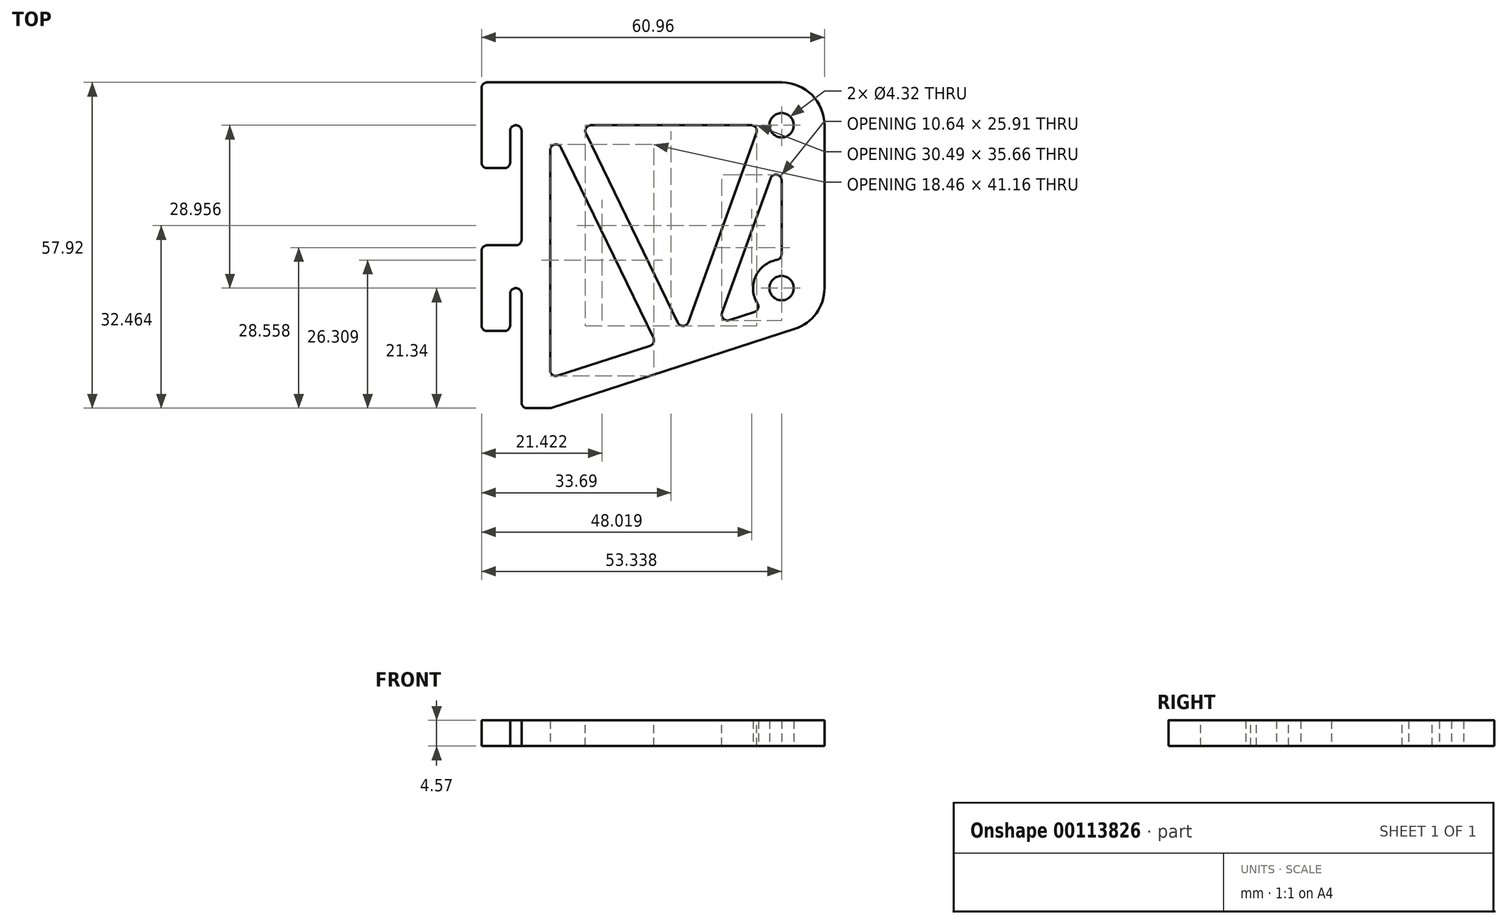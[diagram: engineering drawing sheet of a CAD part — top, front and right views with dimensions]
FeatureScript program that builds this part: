
annotation { "Feature Type Name" : "Feature", "Feature Type Description" : "" }
export const myFeature = defineFeature(function(context is Context, id is Id, definition is map)
    precondition{}
    {
        {
            var Q0;
            Q0=qCreatedBy(makeId("Top.planeOp"),FACE);
            var sketch = newSketch(context, id + "F0", { "sketchPlane" : qUnion([Q0])});
            skLineSegment(sketch, "E0", {"start": v(-7.11, 28.96) * mm, "end": v(-7.11, 13.72) * mm});
            skLineSegment(sketch, "E1", {"start": v(-7.11, 13.72) * mm, "end": v(-2.03, 13.72) * mm});
            skLineSegment(sketch, "E2", {"start": v(-2.03, 13.72) * mm, "end": v(-2.03, 21.34) * mm});
            skLineSegment(sketch, "E3", {"start": v(-2.03, 21.34) * mm, "end": v(0, 21.34) * mm});
            skLineSegment(sketch, "E4", {"start": v(0, 21.34) * mm, "end": v(0, 0) * mm});
            skLineSegment(sketch, "E5", {"start": v(0, 0) * mm, "end": v(-7.11, 0) * mm});
            skLineSegment(sketch, "E6", {"start": v(-7.11, 0) * mm, "end": v(-7.11, -15.24) * mm});
            skLineSegment(sketch, "E7", {"start": v(-7.11, -15.24) * mm, "end": v(-2.03, -15.24) * mm});
            skLineSegment(sketch, "E8", {"start": v(-2.03, -15.24) * mm, "end": v(-2.03, -7.62) * mm});
            skLineSegment(sketch, "E9", {"start": v(-2.03, -7.62) * mm, "end": v(0, -7.62) * mm});
            skLineSegment(sketch, "E10", {"start": v(0, -7.62) * mm, "end": v(0, -28.96) * mm});
            skPoint(sketch, "E11", {"position": v(0, 0) * mm});
            skPoint(sketch, "E12", {"position": v(-7.11, 21.34) * mm});
            skLineSegment(sketch, "E13", {"start": v(-7.11, 28.96) * mm, "end": v(46.23, 28.96) * mm});
            skLineSegment(sketch, "E14", {"start": v(0, -28.96) * mm, "end": v(5.08, -28.96) * mm});
            skLineSegment(sketch, "E15", {"start": v(5.08, -28.96) * mm, "end": v(48.58, -14.87) * mm});
            skCircle(sketch, "E16", {"center": v(46.23, 21.34) * mm, "radius": 2.16 * mm});
            skCircle(sketch, "E17", {"center": v(46.23, -7.62) * mm, "radius": 2.16 * mm});
            skLineSegment(sketch, "E18", {"start": v(46.23, 21.34) * mm, "end": v(46.23, 28.96) * mm, "construction": true});
            skLineSegment(sketch, "E19", {"start": v(46.23, 21.34) * mm, "end": v(53.85, 21.34) * mm, "construction": true});
            skArc(sketch, "E20", {"start": v(53.85, 21.34) * mm, "mid": v(51.62, 26.72) * mm, "end": v(46.23, 28.96) * mm});
            skLineSegment(sketch, "E21", {"start": v(53.85, 21.34) * mm, "end": v(53.85, -7.62) * mm});
            skLineSegment(sketch, "E22", {"start": v(53.85, -7.62) * mm, "end": v(46.23, -7.62) * mm, "construction": true});
            skLineSegment(sketch, "E23", {"start": v(48.58, -14.87) * mm, "end": v(46.23, -7.62) * mm, "construction": true});
            skArc(sketch, "E24", {"start": v(48.58, -14.87) * mm, "mid": v(52.4, -12.1) * mm, "end": v(53.85, -7.62) * mm});
            skLineSegment(sketch, "E25", {"start": v(5.08, 21.34) * mm, "end": v(5.08, -23.62) * mm});
            skPoint(sketch, "E25.startSnap0", {"position": v(-1.02, 21.34) * mm});
            skLineSegment(sketch, "E26", {"start": v(5.08, -23.62) * mm, "end": v(23.95, -17.5) * mm});
            skLineSegment(sketch, "E27", {"start": v(23.95, -17.5) * mm, "end": v(5.08, 21.34) * mm});
            skLineSegment(sketch, "E28", {"start": v(10.73, 21.34) * mm, "end": v(28.83, -15.92) * mm});
            skLineSegment(sketch, "E29", {"start": v(28.83, -15.92) * mm, "end": v(42.26, 21.34) * mm});
            skLineSegment(sketch, "E30", {"start": v(42.26, 21.34) * mm, "end": v(10.73, 21.34) * mm});
            skLineSegment(sketch, "E31", {"start": v(46.23, -2.54) * mm, "end": v(46.23, 17.37) * mm});
            skLineSegment(sketch, "E32", {"start": v(46.23, 17.37) * mm, "end": v(34.95, -13.94) * mm});
            skLineSegment(sketch, "E33", {"start": v(34.95, -13.94) * mm, "end": v(42.83, -11.4) * mm});
            skArc(sketch, "E34", {"start": v(46.23, -2.54) * mm, "mid": v(41.49, -5.8) * mm, "end": v(42.83, -11.4) * mm});
            skLineSegment(sketch, "E35", {"start": v(5.08, -23.62) * mm, "end": v(42.83, -11.4) * mm, "construction": true});
            skLineSegment(sketch, "E36", {"start": v(15.21, 0.49) * mm, "end": v(19.78, 2.7) * mm, "construction": true});
            skLineSegment(sketch, "E37", {"start": v(35.55, 2.7) * mm, "end": v(40.32, 0.98) * mm, "construction": true});
            skPoint(sketch, "E38", {"position": v(35.55, 2.7) * mm});
            skPoint(sketch, "E39", {"position": v(19.78, 2.7) * mm});
            skLineSegment(sketch, "E40", {"start": v(23.95, -17.5) * mm, "end": v(25.52, -22.34) * mm, "construction": true});
            skLineSegment(sketch, "E41", {"start": v(46.23, 21.34) * mm, "end": v(42.26, 21.34) * mm, "construction": true});
            skLineSegment(sketch, "E42", {"start": v(46.23, 21.34) * mm, "end": v(46.23, 17.37) * mm, "construction": true});
            skSolve(sketch);
        }
        {
            var Q0;
            Q0 = qSketchRegion(id + "F0", true);
            extrude(context, id + "F1", {"entities" : qUnion([Q0]), "depth" : 4.57 * mm});
        }
        {
            var Q0;
            Q0=makeQuery(id+"F1.opExtrude","SWEPT_EDGE",EDGE,{"disambiguationData":[OSD([sQuery(id+"F0.wireOp",EDGE,"E31"),sQuery(id+"F0.wireOp",EDGE,"E32")])]});
            var Q1;
            Q1=makeQuery(id+"F1.opExtrude","SWEPT_EDGE",EDGE,{"disambiguationData":[OSD([sQuery(id+"F0.wireOp",EDGE,"E25"),sQuery(id+"F0.wireOp",EDGE,"E27")])]});
            var Q2;
            Q2=makeQuery(id+"F1.opExtrude","SWEPT_EDGE",EDGE,{"disambiguationData":[OSD([sQuery(id+"F0.wireOp",EDGE,"E28"),sQuery(id+"F0.wireOp",EDGE,"E30")])]});
            var Q3;
            Q3=makeQuery(id+"F1.opExtrude","SWEPT_EDGE",EDGE,{"disambiguationData":[OSD([sQuery(id+"F0.wireOp",EDGE,"E29"),sQuery(id+"F0.wireOp",EDGE,"E30")])]});
            var Q4;
            Q4=makeQuery(id+"F1.opExtrude","SWEPT_EDGE",EDGE,{"disambiguationData":[OSD([sQuery(id+"F0.wireOp",EDGE,"E26"),sQuery(id+"F0.wireOp",EDGE,"E27")])]});
            var Q5;
            Q5=makeQuery(id+"F1.opExtrude","SWEPT_EDGE",EDGE,{"disambiguationData":[OSD([sQuery(id+"F0.wireOp",EDGE,"E25"),sQuery(id+"F0.wireOp",EDGE,"E26")])]});
            var Q6;
            Q6=makeQuery(id+"F1.opExtrude","SWEPT_EDGE",EDGE,{"disambiguationData":[OSD([sQuery(id+"F0.wireOp",EDGE,"E28"),sQuery(id+"F0.wireOp",EDGE,"E29")])]});
            var Q7;
            Q7=makeQuery(id+"F1.opExtrude","SWEPT_EDGE",EDGE,{"disambiguationData":[OSD([sQuery(id+"F0.wireOp",EDGE,"E31"),sQuery(id+"F0.wireOp",EDGE,"E34")])]});
            var Q8;
            Q8=makeQuery(id+"F1.opExtrude","SWEPT_EDGE",EDGE,{"disambiguationData":[OSD([sQuery(id+"F0.wireOp",EDGE,"E33"),sQuery(id+"F0.wireOp",EDGE,"E34")])]});
            var Q9;
            Q9=makeQuery(id+"F1.opExtrude","SWEPT_EDGE",EDGE,{"disambiguationData":[OSD([sQuery(id+"F0.wireOp",EDGE,"E32"),sQuery(id+"F0.wireOp",EDGE,"E33")])]});
            var Q10;
            Q10=makeQuery(id+"F1.opExtrude","SWEPT_EDGE",EDGE,{"disambiguationData":[OSD([sQuery(id+"F0.wireOp",EDGE,"E14"),sQuery(id+"F0.wireOp",EDGE,"E15")])]});
            var Q11;
            Q11=makeQuery(id+"F1.opExtrude","SWEPT_EDGE",EDGE,{"disambiguationData":[OSD([sQuery(id+"F0.wireOp",EDGE,"E10"),sQuery(id+"F0.wireOp",EDGE,"E14")])]});
            var Q12;
            Q12=makeQuery(id+"F1.opExtrude","SWEPT_EDGE",EDGE,{"disambiguationData":[OSD([sQuery(id+"F0.wireOp",EDGE,"E9"),sQuery(id+"F0.wireOp",EDGE,"E10")])]});
            var Q13;
            Q13=makeQuery(id+"F1.opExtrude","SWEPT_EDGE",EDGE,{"disambiguationData":[OSD([sQuery(id+"F0.wireOp",EDGE,"E8"),sQuery(id+"F0.wireOp",EDGE,"E9")])]});
            var Q14;
            Q14=makeQuery(id+"F1.opExtrude","SWEPT_EDGE",EDGE,{"disambiguationData":[OSD([sQuery(id+"F0.wireOp",EDGE,"E7"),sQuery(id+"F0.wireOp",EDGE,"E8")])]});
            var Q15;
            Q15=makeQuery(id+"F1.opExtrude","SWEPT_EDGE",EDGE,{"disambiguationData":[OSD([sQuery(id+"F0.wireOp",EDGE,"E6"),sQuery(id+"F0.wireOp",EDGE,"E7")])]});
            var Q16;
            Q16=makeQuery(id+"F1.opExtrude","SWEPT_EDGE",EDGE,{"disambiguationData":[OSD([sQuery(id+"F0.wireOp",EDGE,"E3"),sQuery(id+"F0.wireOp",EDGE,"E4")])]});
            var Q17;
            Q17=makeQuery(id+"F1.opExtrude","SWEPT_EDGE",EDGE,{"disambiguationData":[OSD([sQuery(id+"F0.wireOp",EDGE,"E1"),sQuery(id+"F0.wireOp",EDGE,"E2")])]});
            var Q18;
            Q18=makeQuery(id+"F1.opExtrude","SWEPT_EDGE",EDGE,{"disambiguationData":[OSD([sQuery(id+"F0.wireOp",EDGE,"E0"),sQuery(id+"F0.wireOp",EDGE,"E1")])]});
            var Q19;
            Q19=makeQuery(id+"F1.opExtrude","SWEPT_EDGE",EDGE,{"disambiguationData":[OSD([sQuery(id+"F0.wireOp",EDGE,"E5"),sQuery(id+"F0.wireOp",EDGE,"E6")])]});
            var Q20;
            Q20=makeQuery(id+"F1.opExtrude","SWEPT_EDGE",EDGE,{"disambiguationData":[OSD([sQuery(id+"F0.wireOp",EDGE,"E4"),sQuery(id+"F0.wireOp",EDGE,"E5")])]});
            var Q21;
            Q21=makeQuery(id+"F1.opExtrude","SWEPT_EDGE",EDGE,{"disambiguationData":[OSD([sQuery(id+"F0.wireOp",EDGE,"E2"),sQuery(id+"F0.wireOp",EDGE,"E3")])]});
            var Q22;
            Q22=makeQuery(id+"F1.opExtrude","SWEPT_EDGE",EDGE,{"disambiguationData":[OSD([sQuery(id+"F0.wireOp",EDGE,"E0"),sQuery(id+"F0.wireOp",EDGE,"E13")])]});
            fillet(context, id + "F2", {"entities" : qUnion([Q0, Q1, Q2, Q3, Q4, Q5, Q6, Q7, Q8, Q9, Q10, Q11, Q12, Q13, Q14, Q15, Q16, Q17, Q18, Q19, Q20, Q21, Q22]), "radius" : 1.02 * mm, "tangentPropagation" : true, "allowEdgeOverflow" : false});
        }
    });
